# Revit family: 6220_Eisenrohranschluß flachdichtend (4004,4315,4325,4415,...)
name_source: partatom
category: Rohrformteile
units: mm (PartAtom-declared; Revit-internal decimal feet)

## family parameters
Arbeitsebenenbasiert = Nein
Beim Laden mit Abzugskörper schneiden = Nein
Bemaßung runder Anschluss = Durchmesser verwenden
Gemeinsam genutzt = Nein
Immer vertikal = Ja
OmniClass-Nummer = 23.65.55.14
OmniClass-Titel = Valves for Liquid Services
Teiletyp = Verbindung

## types (5) — shared parameters
Ausführung = Eisenrohranschluss flachdichtend, Mutter und Anschlussstück.
Flachdichtung = Klinger SIL- C4400
Hersteller = HERZ Armaturen Ges.m.b.H.
Max. Betriebsdruck = 1000000.0 Pa
Max. Betriebstemperatur = 110 °C
Medium = Heizungswasser nach ÖNORM H5195 oder VDI- Richtlinie 2035.
Die Verwendung von Ethylen- oder Propyleneglykol in einem Mischungsverhältnis 25- 50% ist zulässig.
Mutter = Messing CW614N, vernickelt
S02 = 8 mm  [stored 0.0262467 ft]
SCRNCODE = 07;01;02
SCRNSEQ = AWI;AWI_TYP="1001";2
URL = www.herz-armaturen.at
Verschraubung = Messing CW614N, vernickelt
zero-valued in all types: Vorgabe-Ansicht

## per-type parameters (varying)
| type | 19_8x2 | 1x3_4 | 3_4x1_2 | 5_4x1 | 7_4x3_2 | Bestellnummer |
| G3/4 x R1/2 | Nein | Nein | Ja | Nein | Nein | 1622011 |
| G1 x R3/4 | Nein | Ja | Nein | Nein | Nein | 1622022 |
| G1 1/4 x R1 | Nein | Nein | Nein | Ja | Nein | 1622063 |
| G1 3/4 x R1 1/2 | Nein | Nein | Nein | Nein | Ja | 1622065 |
| G2 3/8 x R2 | Ja | Nein | Nein | Nein | Nein | 1622066 |

note: [stored X ft] marks values corroborated as IEEE doubles in the binary element streams (Revit-internal decimal feet)
